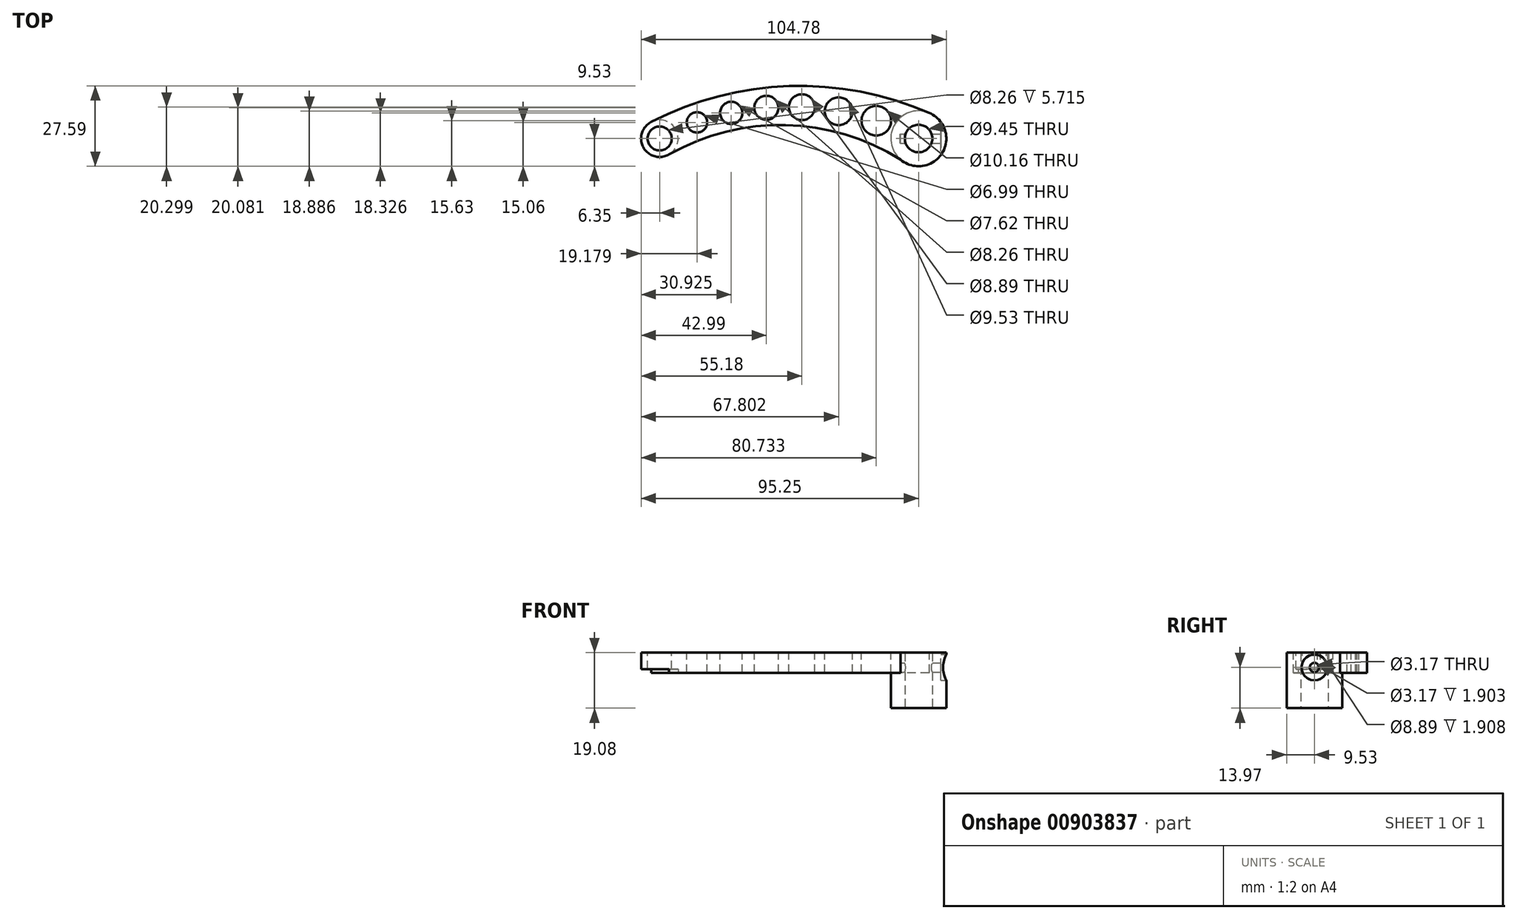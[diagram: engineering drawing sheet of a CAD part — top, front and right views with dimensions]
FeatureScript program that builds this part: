
annotation { "Feature Type Name" : "Feature", "Feature Type Description" : "" }
export const myFeature = defineFeature(function(context is Context, id is Id, definition is map)
    precondition{}
    {
        {
            var Q0;
            Q0=qCreatedBy(makeId("Top.planeOp"),FACE);
            var sketch = newSketch(context, id + "F0", { "sketchPlane" : qUnion([Q0])});
            skCircle(sketch, "E0", {"center": v(0, 0) * mm, "radius": 4.72 * mm});
            skCircle(sketch, "E1", {"center": v(0, 0) * mm, "radius": 9.53 * mm});
            skSolve(sketch);
        }
        {
            var Q0;
            Q0=makeQuery(id+"F0.imprint","IMPRINT",FACE,{"disambiguationData":[TD([[makeQuery(id+"F0.imprint","IMPRINT",EDGE,{"derivedFrom":sQuery(id+"F0.wireOp",EDGE,"E0")}),-1.0]])]});
            extrude(context, id + "F1", {"entities" : qUnion([Q0]), "depth" : 19.08 * mm, "offsetDistance" : 25.4 * mm});
        }
        {
            var Q0;
            Q0=makeQuery(id+"F1.opExtrude","CAP_FACE",FACE,{"disambiguationData":[OSD([sQuery(id+"F0.wireOp",EDGE,"E0"),sQuery(id+"F0.wireOp",EDGE,"E1")])],"isStart":false});
            var sketch = newSketch(context, id + "F2", { "sketchPlane" : qUnion([Q0])});
            skCircle(sketch, "E2", {"center": v(0, 0) * mm, "radius": 9.53 * mm});
            skCircle(sketch, "E3", {"center": v(-88.9, 0) * mm, "radius": 6.35 * mm});
            skCircle(sketch, "E4", {"center": v(-88.9, 0) * mm, "radius": 4.13 * mm});
            skCircle(sketch, "E5.1.0.0", {"center": v(-76.07, 5.53) * mm, "radius": 3.5 * mm});
            skCircle(sketch, "E5.2.0.0", {"center": v(-64.32, 8.8) * mm, "radius": 3.81 * mm});
            skCircle(sketch, "E5.3.0.0", {"center": v(-52.26, 10.55) * mm, "radius": 4.13 * mm});
            skCircle(sketch, "E5.4.0.0", {"center": v(-40.07, 10.77) * mm, "radius": 4.45 * mm});
            skCircle(sketch, "E6.0.5.0", {"center": v(-27.45, 9.36) * mm, "radius": 4.76 * mm});
            skCircle(sketch, "E7.0.6.0", {"center": v(-14.52, 6.1) * mm, "radius": 5.08 * mm});
            skArc(sketch, "E8", {"start": v(3.68, 8.79) * mm, "mid": v(-44.39, 18) * mm, "end": v(-91.75, 5.68) * mm});
            skArc(sketch, "E9", {"start": v(-6.17, -7.26) * mm, "mid": v(-45.78, 4.62) * mm, "end": v(-85.86, -5.58) * mm});
            skArc(sketch, "E10", {"start": v(0, 0) * mm, "mid": v(-44.45, 10.87) * mm, "end": v(-88.9, 0) * mm});
            skSolve(sketch);
        }
        {
            var Q0;
            Q0=qSketchRegion(id+"F2",true);
            extrude(context, id + "F3", {"entities" : qUnion([Q0]), "operationType" : NewBodyOperationType.ADD, "oppositeDirection" : true, "depth" : 7 * mm, "offsetDistance" : 25.4 * mm});
        }
        {
            var Q0;
            Q0=qCreatedBy(makeId("Right.planeOp"),FACE);
            cPlane(context, id + "F4", {"entities" : qUnion([Q0]), "cplaneType" : CPlaneType.OFFSET, "offset" : 25.4 * mm, "width" : 152.4 * mm, "height" : 152.4 * mm});
        }
        {
            var Q0;
            Q0=qCreatedBy(id+"F4.planeOp",FACE);
            var sketch = newSketch(context, id + "F5", { "sketchPlane" : qUnion([Q0])});
            skLineSegment(sketch, "E11", {"start": v(0, 0) * mm, "end": v(0, 13.97) * mm, "construction": true});
            skCircle(sketch, "E12", {"center": v(0, 13.97) * mm, "radius": 1.59 * mm});
            skCircle(sketch, "E13", {"center": v(0, 13.97) * mm, "radius": 4.45 * mm});
            skSolve(sketch);
        }
        {
            var Q0;
            Q0=makeQuery(id+"F5.imprint","IMPRINT",FACE,{"disambiguationData":[TD([[makeQuery(id+"F5.imprint","IMPRINT",EDGE,{"derivedFrom":sQuery(id+"F5.wireOp",EDGE,"E12")}),1.0]])]});
            extrude(context, id + "F6", {"entities" : qUnion([Q0]), "operationType" : NewBodyOperationType.REMOVE, "oppositeDirection" : true, "depth" : 31.75 * mm, "offsetDistance" : 25.4 * mm});
        }
        {
            var Q0;
            Q0=makeQuery(id+"F0.imprint","IMPRINT",FACE,{"disambiguationData":[TD([[makeQuery(id+"F0.imprint","IMPRINT",EDGE,{"derivedFrom":sQuery(id+"F0.wireOp",EDGE,"E0")}),1.0]])]});
            extrude(context, id + "F7", {"entities" : qUnion([Q0]), "operationType" : NewBodyOperationType.REMOVE, "depth" : 25.4 * mm, "offsetDistance" : 25.4 * mm});
        }
        {
            var Q0;
            {var subQ0=sQuery(id+"F2.wireOp",EDGE,"E5.4.0.0");var subQ1=sQuery(id+"F2.wireOp",EDGE,"E5.3.0.0");var subQ2=sQuery(id+"F2.wireOp",EDGE,"E5.1.0.0");var subQ3=sQuery(id+"F2.wireOp",EDGE,"E4");var subQ4=sQuery(id+"F2.wireOp",EDGE,"pdIjIbcP-9SOD-l8nC-nuJ8-Q8D78OAUkfvr");var subQ5=sQuery(id+"F2.wireOp",EDGE,"E5.2.0.0");var subQ6=sQuery(id+"F2.wireOp",EDGE,"shAArMzN-EGuV-3dkC-qGel-LoSvuiHDjsw2");var subQ7=sQuery(id+"F2.wireOp",EDGE,"E3");var subQ8=sQuery(id+"F2.wireOp",EDGE,"RlJzC9K9-Zykr-zV44-zTBI-Gw15smUKGiue");var subQ9=sQuery(id+"F2.wireOp",EDGE,"E6.0.5.0");Q0=makeQuery(id+"F3.boolean.opBoolean","SPLIT",FACE,{"disambiguationData":[TD([makeQuery(id+"F1.opExtrude","SWEPT_FACE",FACE,{"disambiguationData":[OSD([sQuery(id+"F0.wireOp",EDGE,"E1")])]})])],"derivedFrom":makeQuery(id+"F3.opExtrude","CAP_FACE",FACE,{"disambiguationData":[OSD([sQuery(id+"F2.wireOp",EDGE,"E2"),subQ7,subQ6,subQ8,subQ4,subQ3,subQ2,subQ5,subQ1,subQ0,subQ9])],"isStart":false})});}
            var sketch = newSketch(context, id + "F8", { "sketchPlane" : qUnion([Q0])});
            skCircle(sketch, "E14", {"center": v(-88.9, 0) * mm, "radius": 6.35 * mm});
            skSolve(sketch);
        }
        {
            var Q0;
            Q0=qSketchRegion(id+"F8",true);
            extrude(context, id + "F9", {"entities" : qUnion([Q0]), "operationType" : NewBodyOperationType.REMOVE, "oppositeDirection" : true, "depth" : 1.27 * mm, "offsetDistance" : 25.4 * mm});
        }
        {
            var Q0;
            Q0=makeQuery(id+"F5.imprint","IMPRINT",FACE,{"disambiguationData":[TD([[makeQuery(id+"F5.imprint","IMPRINT",EDGE,{"derivedFrom":sQuery(id+"F5.wireOp",EDGE,"E12")}),-1.0]])]});
            extrude(context, id + "F10", {"entities" : qUnion([Q0]), "operationType" : NewBodyOperationType.REMOVE, "oppositeDirection" : true, "depth" : 17.78 * mm, "offsetDistance" : 25.4 * mm});
        }
        {
            var Q0;
            {var subQ0=sQuery(id+"F2.wireOp",EDGE,"RlJzC9K9-Zykr-zV44-zTBI-Gw15smUKGiue");Q0=makeQuery(id+"F9.boolean.opBoolean","SPLIT",EDGE,{"disambiguationData":[topologyDisambiguationEdgeConnected([makeQuery(id+"F9.opExtrude","SWEPT_FACE",FACE,{"disambiguationData":[OSD([sQuery(id+"F8.wireOp",EDGE,"E14")])]})])],"derivedFrom":makeQuery(id+"F3.opExtrude","SWEPT_EDGE",EDGE,{"disambiguationData":[OSD([sQuery(id+"F2.wireOp",EDGE,"E3"),subQ0])]})});}
            var Q1;
            {var subQ0=sQuery(id+"F2.wireOp",EDGE,"shAArMzN-EGuV-3dkC-qGel-LoSvuiHDjsw2");Q1=makeQuery(id+"F9.boolean.opBoolean","SPLIT",EDGE,{"disambiguationData":[topologyDisambiguationEdgeConnected([makeQuery(id+"F9.opExtrude","SWEPT_FACE",FACE,{"disambiguationData":[OSD([sQuery(id+"F8.wireOp",EDGE,"E14")])]})])],"derivedFrom":makeQuery(id+"F3.opExtrude","SWEPT_EDGE",EDGE,{"disambiguationData":[OSD([sQuery(id+"F2.wireOp",EDGE,"E3"),subQ0])]})});}
            fillet(context, id + "F11", {"entities" : qUnion([Q0, Q1]), "tangentPropagation" : true, "radius" : 2.54 * mm, "defaultsChanged" : true, "vertexSettings" : [], "allowEdgeOverflow" : false});
        }
    });
